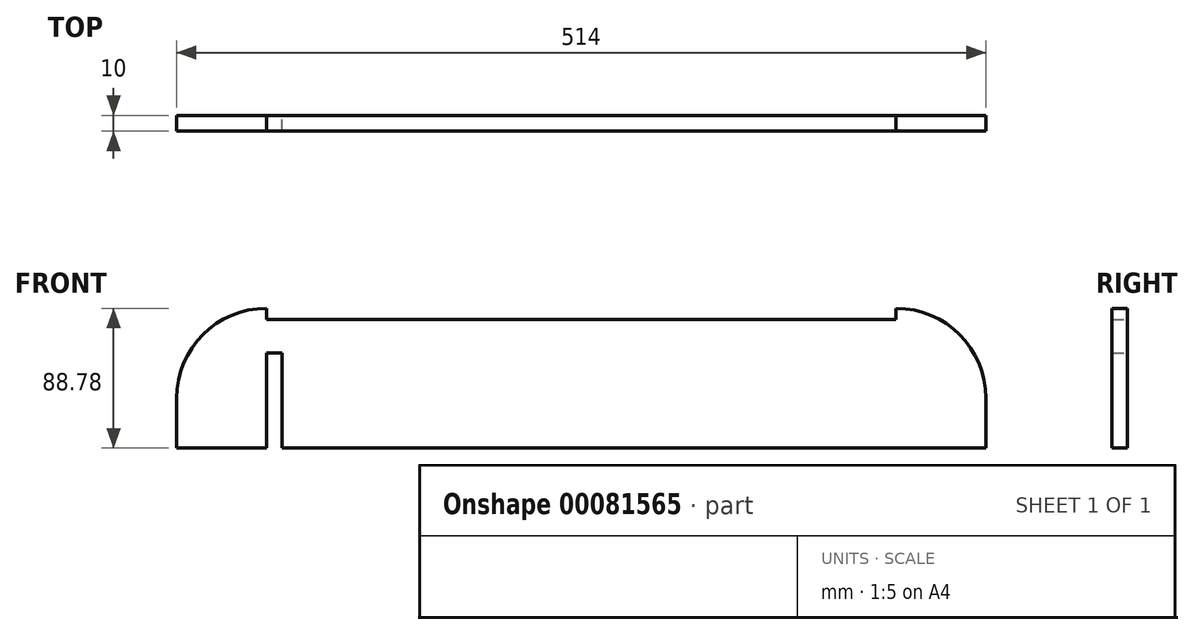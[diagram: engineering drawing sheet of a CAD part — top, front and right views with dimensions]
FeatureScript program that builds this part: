
annotation { "Feature Type Name" : "Feature", "Feature Type Description" : "" }
export const myFeature = defineFeature(function(context is Context, id is Id, definition is map)
    precondition{}
    {
        {
            var Q0;
            Q0=qCreatedBy(makeId("Front.planeOp"),FACE);
            var sketch = newSketch(context, id + "F0", { "sketchPlane" : qUnion([Q0])});
            skLineSegment(sketch, "E0", {"start": v(-200, 57) * mm, "end": v(200, 57) * mm, "construction": true});
            skLineSegment(sketch, "E1", {"start": v(257, 0) * mm, "end": v(200, 0) * mm, "construction": true});
            skArc(sketch, "E2", {"start": v(-200, 57) * mm, "mid": v(-240.3, 40.3) * mm, "end": v(-257, 0) * mm});
            skArc(sketch, "E3", {"start": v(257, 0) * mm, "mid": v(240.3, 40.3) * mm, "end": v(200, 57) * mm});
            skLineSegment(sketch, "E4", {"start": v(-200, 0) * mm, "end": v(-200, 28.5) * mm});
            skLineSegment(sketch, "E5", {"start": v(-200, 28.5) * mm, "end": v(-190, 28.5) * mm});
            skLineSegment(sketch, "E6", {"start": v(-190, 28.5) * mm, "end": v(-190, 0) * mm});
            skLineSegment(sketch, "E7.trimOffspring", {"start": v(-200, 0) * mm, "end": v(-257, 0) * mm, "construction": true});
            skLineSegment(sketch, "E8", {"start": v(200, 0) * mm, "end": v(200, 28.5) * mm, "construction": true});
            skLineSegment(sketch, "E9", {"start": v(200, 28.5) * mm, "end": v(190, 28.5) * mm, "construction": true});
            skLineSegment(sketch, "E10", {"start": v(190, 28.5) * mm, "end": v(190, 0) * mm, "construction": true});
            skLineSegment(sketch, "E11.trimOffspring", {"start": v(190, 0) * mm, "end": v(-190, 0) * mm, "construction": true});
            skLineSegment(sketch, "E12", {"start": v(200, 57) * mm, "end": v(200, 50) * mm});
            skLineSegment(sketch, "E13", {"start": v(200, 50) * mm, "end": v(-200, 50) * mm});
            skLineSegment(sketch, "E14", {"start": v(-200, 50) * mm, "end": v(-200, 57) * mm});
            skLineSegment(sketch, "E15", {"start": v(-257, 0) * mm, "end": v(-257, -31.78) * mm});
            skLineSegment(sketch, "E16", {"start": v(-257, -31.78) * mm, "end": v(-200, -31.78) * mm});
            skLineSegment(sketch, "E17", {"start": v(-200, -31.78) * mm, "end": v(-200, 0) * mm});
            skLineSegment(sketch, "E18", {"start": v(-190, 0) * mm, "end": v(-190, -31.78) * mm});
            skLineSegment(sketch, "E19", {"start": v(-190, -31.78) * mm, "end": v(190, -31.78) * mm});
            skLineSegment(sketch, "E20", {"start": v(190, -31.78) * mm, "end": v(190, 0) * mm, "construction": true});
            skLineSegment(sketch, "E21", {"start": v(200, 0) * mm, "end": v(200, -31.78) * mm, "construction": true});
            skLineSegment(sketch, "E22", {"start": v(200, -31.78) * mm, "end": v(257, -31.78) * mm});
            skLineSegment(sketch, "E23", {"start": v(257, -31.78) * mm, "end": v(257, 0) * mm});
            skLineSegment(sketch, "E24", {"start": v(190, -31.78) * mm, "end": v(200, -31.78) * mm});
            skSolve(sketch);
        }
        {
            var Q0;
            Q0 = qSketchRegion(id + "F0", true);
            extrude(context, id + "F1", {"entities" : qUnion([Q0]), "depth" : 10 * mm});
        }
    });
